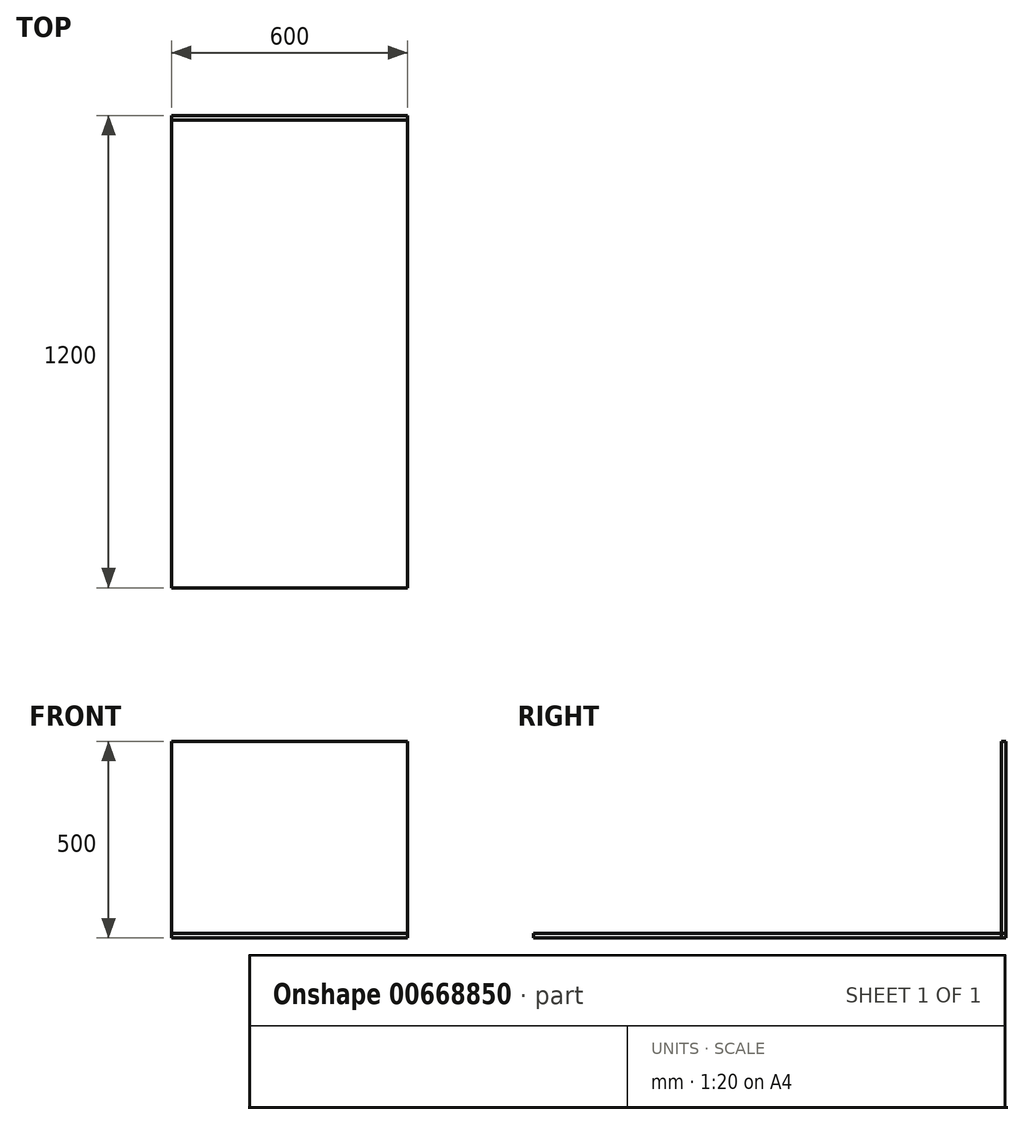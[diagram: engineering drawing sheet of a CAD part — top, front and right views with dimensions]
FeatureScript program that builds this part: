
annotation { "Feature Type Name" : "Feature", "Feature Type Description" : "" }
export const myFeature = defineFeature(function(context is Context, id is Id, definition is map)
    precondition{}
    {
        {
            var Q0;
            Q0=qCreatedBy(makeId("Top.planeOp"),FACE);
            var sketch = newSketch(context, id + "F0", { "sketchPlane" : qUnion([Q0])});
            skLineSegment(sketch, "E0.bottom", {"start": v(-1108.51, 534.49) * mm, "end": v(-508.51, 534.49) * mm});
            skLineSegment(sketch, "E0.top", {"start": v(-1108.51, -665.51) * mm, "end": v(-508.51, -665.51) * mm});
            skLineSegment(sketch, "E0.left", {"start": v(-1108.51, 534.49) * mm, "end": v(-1108.51, -665.51) * mm});
            skLineSegment(sketch, "E0.right", {"start": v(-508.51, 534.49) * mm, "end": v(-508.51, -665.51) * mm});
            skLineSegment(sketch, "E1.bottom", {"start": v(-508.51, 534.49) * mm, "end": v(-508.51, 534.49) * mm});
            skLineSegment(sketch, "E1.top", {"start": v(-508.51, -665.51) * mm, "end": v(-508.51, -665.51) * mm});
            skLineSegment(sketch, "E2.top", {"start": v(-508.51, -609.1) * mm, "end": v(-508.51, -609.1) * mm});
            skLineSegment(sketch, "E2.left", {"start": v(-508.51, 534.49) * mm, "end": v(-508.51, -609.1) * mm});
            skLineSegment(sketch, "E2.right", {"start": v(-508.51, 534.49) * mm, "end": v(-508.51, -609.1) * mm});
            skLineSegment(sketch, "E3.top", {"start": v(-1108.51, 522.49) * mm, "end": v(-508.51, 522.49) * mm});
            skLineSegment(sketch, "E3.left", {"start": v(-1108.51, 534.49) * mm, "end": v(-1108.51, 522.49) * mm});
            skLineSegment(sketch, "E3.right", {"start": v(-508.51, 534.49) * mm, "end": v(-508.51, 522.49) * mm});
            skLineSegment(sketch, "E4.bottom", {"start": v(-508.51, -665.51) * mm, "end": v(-1108.51, -665.51) * mm});
            skLineSegment(sketch, "E4.top", {"start": v(-508.51, -653.51) * mm, "end": v(-1108.51, -653.51) * mm});
            skLineSegment(sketch, "E4.left", {"start": v(-508.51, -665.51) * mm, "end": v(-508.51, -653.51) * mm});
            skLineSegment(sketch, "E4.right", {"start": v(-1108.51, -665.51) * mm, "end": v(-1108.51, -653.51) * mm});
            skSolve(sketch);
        }
        {
            var Q0;
            Q0=makeQuery(id+"F0.imprint","IMPRINT",FACE,{"disambiguationData":[TD([[makeQuery(id+"F0.imprint","IMPRINT",EDGE,{"derivedFrom":sQuery(id+"F0.wireOp",EDGE,"E0.bottom")}),-1.0]])]});
            var Q1;
            Q1=makeQuery(id+"F0.imprint","IMPRINT",FACE,{"disambiguationData":[TD([[makeQuery(id+"F0.imprint","IMPRINT",EDGE,{"derivedFrom":sQuery(id+"F0.wireOp",EDGE,"E4.bottom")}),-1.0]])]});
            extrude(context, id + "F1", {"entities" : qUnion([Q0, Q1]), "depth" : 500 * mm, "offsetDistance" : 25 * mm});
        }
        {
            var Q0;
            Q0=makeQuery(id+"F0.imprint","IMPRINT",FACE,{"disambiguationData":[TD([[makeQuery(id+"F0.imprint","IMPRINT",EDGE,{"derivedFrom":sQuery(id+"F0.wireOp",EDGE,"E0.left")}),1.0]])]});
            extrude(context, id + "F2", {"entities" : qUnion([Q0]), "depth" : 12 * mm, "offsetDistance" : 25 * mm});
        }
    });
